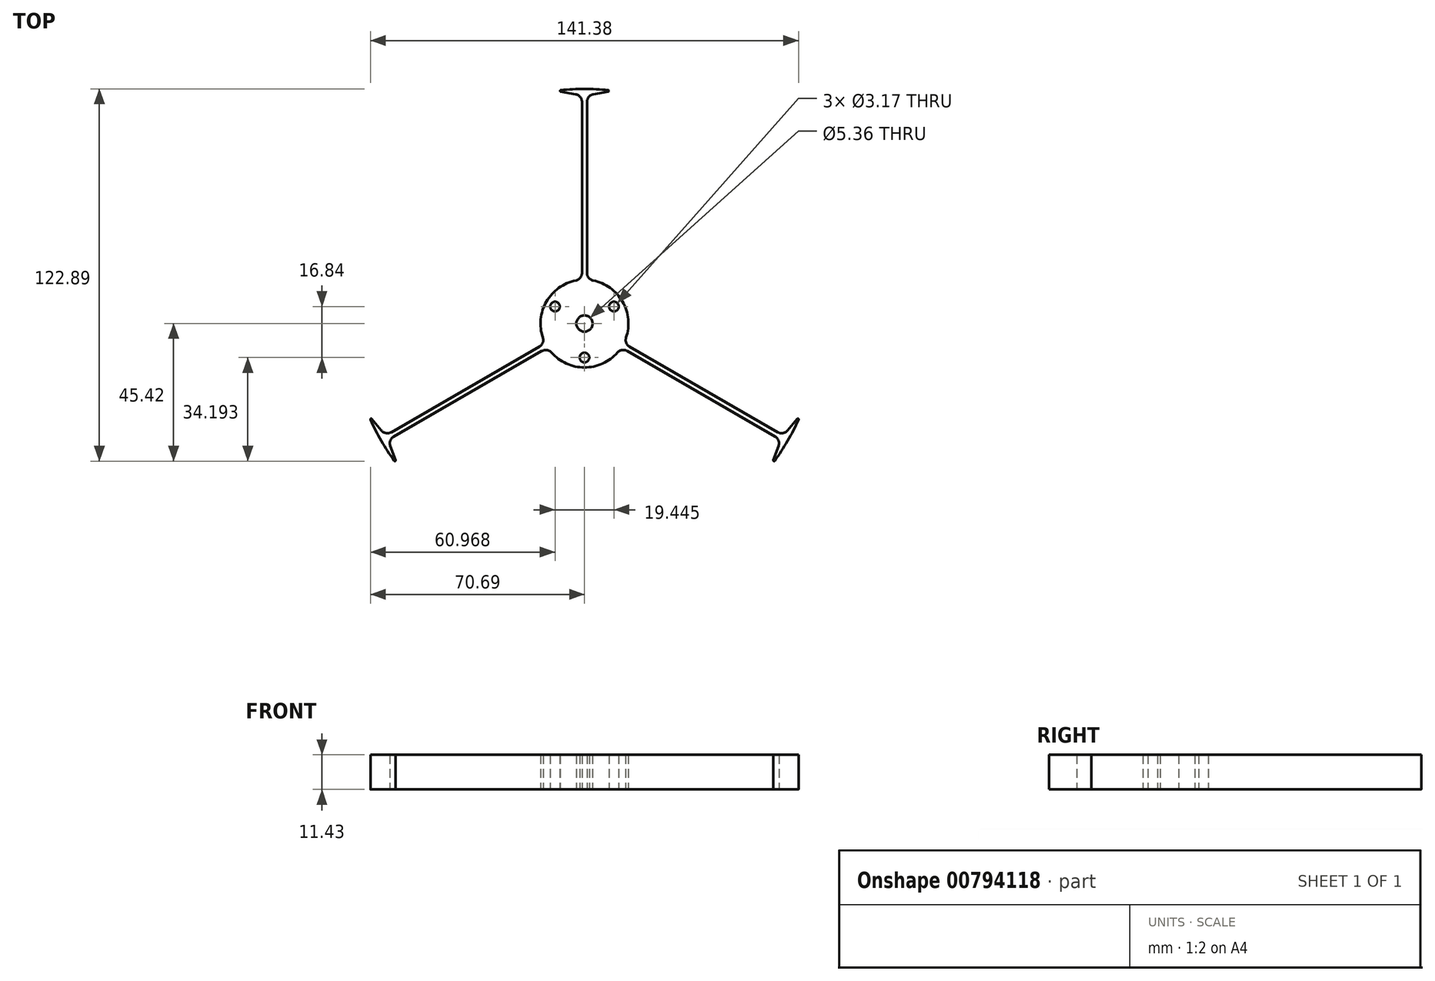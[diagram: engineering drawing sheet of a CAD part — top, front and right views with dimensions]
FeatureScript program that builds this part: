
annotation { "Feature Type Name" : "Feature", "Feature Type Description" : "" }
export const myFeature = defineFeature(function(context is Context, id is Id, definition is map)
    precondition{}
    {
        {
            var Q0;
            Q0=qCreatedBy(makeId("Top.planeOp"),FACE);
            var sketch = newSketch(context, id + "F0", { "sketchPlane" : qUnion([Q0])});
            skCircle(sketch, "E0", {"center": v(0, 0) * mm, "radius": 77.47 * mm});
            skCircle(sketch, "E1", {"center": v(0, 0) * mm, "radius": 14.5 * mm});
            skLineSegment(sketch, "E2", {"start": v(-0.83, 77.47) * mm, "end": v(-0.83, 14.48) * mm});
            skLineSegment(sketch, "E3", {"start": v(0.83, 77.47) * mm, "end": v(0.83, 14.48) * mm});
            skLineSegment(sketch, "E4.1.0", {"start": v(-67.5, -38.02) * mm, "end": v(-12.95, -6.52) * mm});
            skLineSegment(sketch, "E4.1.1", {"start": v(-66.67, -39.45) * mm, "end": v(-12.12, -7.95) * mm});
            skLineSegment(sketch, "E4.2.0", {"start": v(66.67, -39.45) * mm, "end": v(12.12, -7.95) * mm});
            skLineSegment(sketch, "E4.2.1", {"start": v(67.5, -38.02) * mm, "end": v(12.95, -6.52) * mm});
            skCircle(sketch, "E5", {"center": v(0, 0) * mm, "radius": 2.68 * mm});
            skLineSegment(sketch, "E6", {"start": v(0.83, 14.48) * mm, "end": v(12.95, -6.52) * mm, "construction": true});
            skLineSegment(sketch, "E7", {"start": v(6.89, 3.98) * mm, "end": v(12.56, 7.25) * mm, "construction": true});
            skCircle(sketch, "E8", {"center": v(9.72, 5.61) * mm, "radius": 1.59 * mm});
            skCircle(sketch, "E9.1.0", {"center": v(-9.72, 5.61) * mm, "radius": 1.59 * mm});
            skCircle(sketch, "E9.2.0", {"center": v(0, -11.23) * mm, "radius": 1.59 * mm});
            skLineSegment(sketch, "E10", {"start": v(-0.83, 75.33) * mm, "end": v(-9.58, 76.88) * mm});
            skLineSegment(sketch, "E11", {"start": v(0.83, 75.33) * mm, "end": v(9.58, 76.88) * mm});
            skLineSegment(sketch, "E12.1.0", {"start": v(-65.65, -36.95) * mm, "end": v(-71.37, -30.14) * mm});
            skLineSegment(sketch, "E12.1.1", {"start": v(-64.83, -38.38) * mm, "end": v(-61.79, -46.73) * mm});
            skLineSegment(sketch, "E12.2.0", {"start": v(64.83, -38.38) * mm, "end": v(61.79, -46.73) * mm});
            skLineSegment(sketch, "E12.2.1", {"start": v(65.65, -36.95) * mm, "end": v(71.37, -30.14) * mm});
            skSolve(sketch);
        }
        {
            var Q0;
            Q0=makeQuery(id+"F0.imprint","IMPRINT",FACE,{"disambiguationData":[TD([[makeQuery(id+"F0.imprint","IMPRINT",EDGE,{"derivedFrom":sQuery(id+"F0.wireOp",EDGE,"E5")}),-1.0]])]});
            var Q1;
            {var subQ0=sQuery(id+"F0.wireOp",EDGE,"E2");Q1=makeQuery(id+"F0.imprint","IMPRINT",FACE,{"disambiguationData":[TD([[makeQuery(id+"F0.imprint","IMPRINT",EDGE,{"derivedFrom":subQ0}),1.0]])]});}
            var Q2;
            {var subQ0=sQuery(id+"F0.wireOp",EDGE,"E4.1.0");Q2=makeQuery(id+"F0.imprint","IMPRINT",FACE,{"disambiguationData":[TD([[makeQuery(id+"F0.imprint","IMPRINT",EDGE,{"derivedFrom":subQ0}),-1.0]])]});}
            var Q3;
            {var subQ0=sQuery(id+"F0.wireOp",EDGE,"E4.2.0");Q3=makeQuery(id+"F0.imprint","IMPRINT",FACE,{"disambiguationData":[TD([[makeQuery(id+"F0.imprint","IMPRINT",EDGE,{"derivedFrom":subQ0}),-1.0]])]});}
            var Q4;
            {var subQ3=sQuery(id+"F0.wireOp",EDGE,"E10");Q4=makeQuery(id+"F0.imprint","IMPRINT",FACE,{"disambiguationData":[TD([[makeQuery(id+"F0.imprint","IMPRINT",EDGE,{"derivedFrom":subQ3}),-1.0]])]});}
            var Q5;
            {var subQ3=sQuery(id+"F0.wireOp",EDGE,"E11");Q5=makeQuery(id+"F0.imprint","IMPRINT",FACE,{"disambiguationData":[TD([[makeQuery(id+"F0.imprint","IMPRINT",EDGE,{"derivedFrom":subQ3}),1.0]])]});}
            var Q6;
            {var subQ3=sQuery(id+"F0.wireOp",EDGE,"E12.2.0");Q6=makeQuery(id+"F0.imprint","IMPRINT",FACE,{"disambiguationData":[TD([[makeQuery(id+"F0.imprint","IMPRINT",EDGE,{"derivedFrom":subQ3}),1.0]])]});}
            var Q7;
            {var subQ3=sQuery(id+"F0.wireOp",EDGE,"E12.2.1");Q7=makeQuery(id+"F0.imprint","IMPRINT",FACE,{"disambiguationData":[TD([[makeQuery(id+"F0.imprint","IMPRINT",EDGE,{"derivedFrom":subQ3}),-1.0]])]});}
            var Q8;
            {var subQ3=sQuery(id+"F0.wireOp",EDGE,"E12.1.1");Q8=makeQuery(id+"F0.imprint","IMPRINT",FACE,{"disambiguationData":[TD([[makeQuery(id+"F0.imprint","IMPRINT",EDGE,{"derivedFrom":subQ3}),-1.0]])]});}
            var Q9;
            {var subQ3=sQuery(id+"F0.wireOp",EDGE,"E12.1.0");Q9=makeQuery(id+"F0.imprint","IMPRINT",FACE,{"disambiguationData":[TD([[makeQuery(id+"F0.imprint","IMPRINT",EDGE,{"derivedFrom":subQ3}),1.0]])]});}
            extrude(context, id + "F1", {"entities" : qUnion([Q0, Q1, Q2, Q3, Q4, Q5, Q6, Q7, Q8, Q9]), "depth" : 11.43 * mm, "offsetDistance" : 25.4 * mm});
        }
        {
            var Q0;
            Q0=makeQuery(id+"F1.opExtrude","SWEPT_EDGE",EDGE,{"disambiguationData":[OSD([sQuery(id+"F0.wireOp",EDGE,"E0"),sQuery(id+"F0.wireOp",EDGE,"E12.2.1")])]});
            var Q1;
            Q1=makeQuery(id+"F1.opExtrude","SWEPT_EDGE",EDGE,{"disambiguationData":[OSD([sQuery(id+"F0.wireOp",EDGE,"E0"),sQuery(id+"F0.wireOp",EDGE,"E12.2.0")])]});
            var Q2;
            Q2=makeQuery(id+"F1.opExtrude","SWEPT_EDGE",EDGE,{"disambiguationData":[OSD([sQuery(id+"F0.wireOp",EDGE,"E0"),sQuery(id+"F0.wireOp",EDGE,"E12.1.0")])]});
            var Q3;
            Q3=makeQuery(id+"F1.opExtrude","SWEPT_EDGE",EDGE,{"disambiguationData":[OSD([sQuery(id+"F0.wireOp",EDGE,"E0"),sQuery(id+"F0.wireOp",EDGE,"E12.1.1")])]});
            var Q4;
            Q4=makeQuery(id+"F1.opExtrude","SWEPT_EDGE",EDGE,{"disambiguationData":[OSD([sQuery(id+"F0.wireOp",EDGE,"E0"),sQuery(id+"F0.wireOp",EDGE,"E10")])]});
            var Q5;
            Q5=makeQuery(id+"F1.opExtrude","SWEPT_EDGE",EDGE,{"disambiguationData":[OSD([sQuery(id+"F0.wireOp",EDGE,"E0"),sQuery(id+"F0.wireOp",EDGE,"E11")])]});
            fillet(context, id + "F2", {"entities" : qUnion([Q0, Q1, Q2, Q3, Q4, Q5]), "radius" : 0.25 * mm, "tangentPropagation" : true, "allowEdgeOverflow" : false});
        }
        {
            var Q0;
            Q0=makeQuery(id+"F1.opExtrude","SWEPT_EDGE",EDGE,{"disambiguationData":[OSD([sQuery(id+"F0.wireOp",EDGE,"E1"),sQuery(id+"F0.wireOp",EDGE,"E4.1.1")])]});
            var Q1;
            Q1=makeQuery(id+"F1.opExtrude","SWEPT_EDGE",EDGE,{"disambiguationData":[OSD([sQuery(id+"F0.wireOp",EDGE,"E1"),sQuery(id+"F0.wireOp",EDGE,"E4.1.0")])]});
            var Q2;
            Q2=makeQuery(id+"F1.opExtrude","SWEPT_EDGE",EDGE,{"disambiguationData":[OSD([sQuery(id+"F0.wireOp",EDGE,"E1"),sQuery(id+"F0.wireOp",EDGE,"E2")])]});
            var Q3;
            Q3=makeQuery(id+"F1.opExtrude","SWEPT_EDGE",EDGE,{"disambiguationData":[OSD([sQuery(id+"F0.wireOp",EDGE,"E1"),sQuery(id+"F0.wireOp",EDGE,"E3")])]});
            var Q4;
            Q4=makeQuery(id+"F1.opExtrude","SWEPT_EDGE",EDGE,{"disambiguationData":[OSD([sQuery(id+"F0.wireOp",EDGE,"E1"),sQuery(id+"F0.wireOp",EDGE,"E4.2.1")])]});
            var Q5;
            Q5=makeQuery(id+"F1.opExtrude","SWEPT_EDGE",EDGE,{"disambiguationData":[OSD([sQuery(id+"F0.wireOp",EDGE,"E1"),sQuery(id+"F0.wireOp",EDGE,"E4.2.0")])]});
            var Q6;
            Q6=makeQuery(id+"F1.opExtrude","SWEPT_EDGE",EDGE,{"disambiguationData":[OSD([sQuery(id+"F0.wireOp",EDGE,"E4.1.1"),sQuery(id+"F0.wireOp",EDGE,"E12.1.1")])]});
            var Q7;
            Q7=makeQuery(id+"F1.opExtrude","SWEPT_EDGE",EDGE,{"disambiguationData":[OSD([sQuery(id+"F0.wireOp",EDGE,"E4.1.0"),sQuery(id+"F0.wireOp",EDGE,"E12.1.0")])]});
            var Q8;
            Q8=makeQuery(id+"F1.opExtrude","SWEPT_EDGE",EDGE,{"disambiguationData":[OSD([sQuery(id+"F0.wireOp",EDGE,"E2"),sQuery(id+"F0.wireOp",EDGE,"E10")])]});
            var Q9;
            Q9=makeQuery(id+"F1.opExtrude","SWEPT_EDGE",EDGE,{"disambiguationData":[OSD([sQuery(id+"F0.wireOp",EDGE,"E4.2.0"),sQuery(id+"F0.wireOp",EDGE,"E12.2.0")])]});
            var Q10;
            Q10=makeQuery(id+"F1.opExtrude","SWEPT_EDGE",EDGE,{"disambiguationData":[OSD([sQuery(id+"F0.wireOp",EDGE,"E4.2.1"),sQuery(id+"F0.wireOp",EDGE,"E12.2.1")])]});
            var Q11;
            Q11=makeQuery(id+"F1.opExtrude","SWEPT_EDGE",EDGE,{"disambiguationData":[OSD([sQuery(id+"F0.wireOp",EDGE,"E3"),sQuery(id+"F0.wireOp",EDGE,"E11")])]});
            fillet(context, id + "F3", {"entities" : qUnion([Q0, Q1, Q2, Q3, Q4, Q5, Q6, Q7, Q8, Q9, Q10, Q11]), "radius" : 2.54 * mm, "tangentPropagation" : true, "allowEdgeOverflow" : false});
        }
    });
